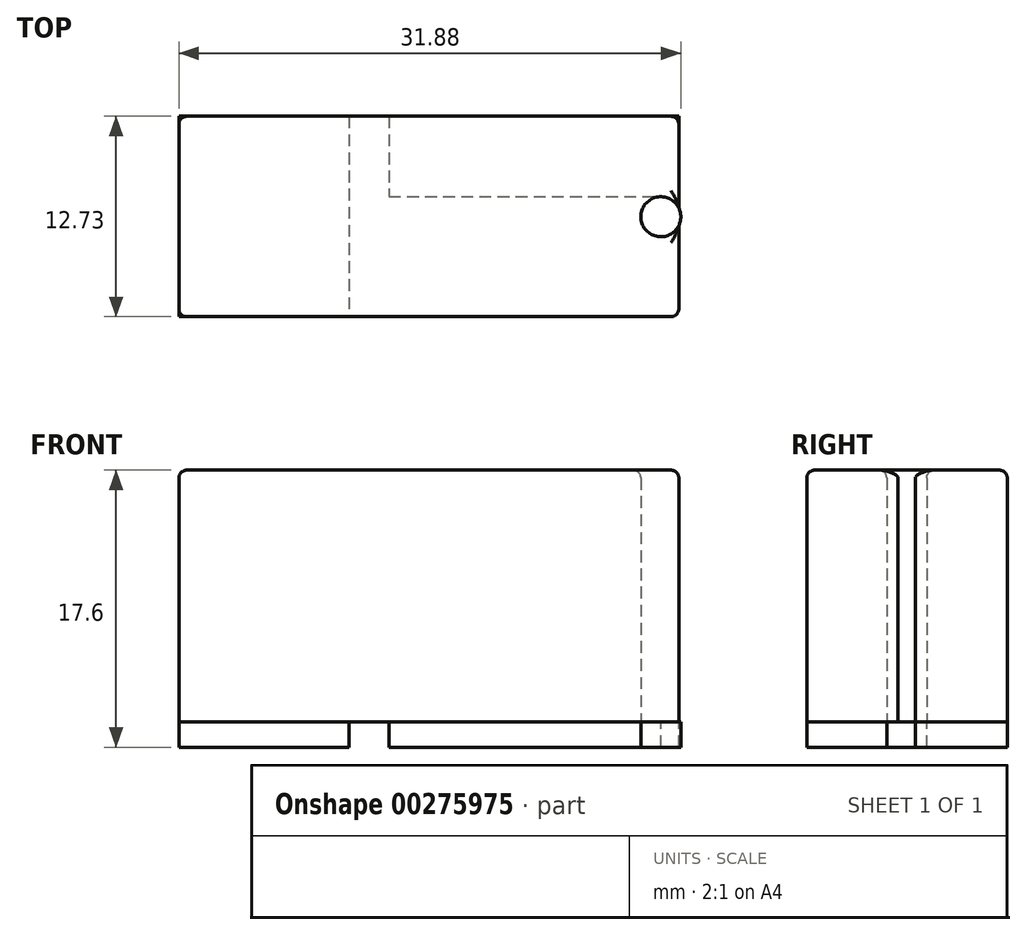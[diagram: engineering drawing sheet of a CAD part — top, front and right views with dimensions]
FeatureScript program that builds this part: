
annotation { "Feature Type Name" : "Feature", "Feature Type Description" : "" }
export const myFeature = defineFeature(function(context is Context, id is Id, definition is map)
    precondition{}
    {
        {
            var Q0;
            Q0=qCreatedBy(makeId("Top.planeOp"),FACE);
            var sketch = newSketch(context, id + "F0", { "sketchPlane" : qUnion([Q0])});
            skLineSegment(sketch, "E0.bottom", {"start": v(-24.13, 16) * mm, "end": v(24.13, 16) * mm});
            skLineSegment(sketch, "E0.top", {"start": v(-24.13, -16) * mm, "end": v(24.13, -16) * mm});
            skLineSegment(sketch, "E0.left", {"start": v(-24.13, 16) * mm, "end": v(-24.13, -16) * mm});
            skLineSegment(sketch, "E0.right", {"start": v(24.13, 16) * mm, "end": v(24.13, -16) * mm});
            skPoint(sketch, "E1", {"position": v(24.13, 0) * mm});
            skPoint(sketch, "E2", {"position": v(0, 16) * mm});
            skSolve(sketch);
        }
        {
            var Q0;
            Q0=makeQuery(id+"F0.imprint","IMPRINT",FACE,{"disambiguationData":[TD([[makeQuery(id+"F0.imprint","IMPRINT",EDGE,{"derivedFrom":sQuery(id+"F0.wireOp",EDGE,"E0.bottom")}),-1.0]])]});
            extrude(context, id + "F1", {"entities" : qUnion([Q0]), "depth" : 1.6 * mm});
        }
        {
            var Q0;
            Q0=makeQuery(id+"F1.opExtrude","CAP_FACE",FACE,{"disambiguationData":[OSD([sQuery(id+"F0.wireOp",EDGE,"E0.bottom"),sQuery(id+"F0.wireOp",EDGE,"E0.top"),sQuery(id+"F0.wireOp",EDGE,"E0.left"),sQuery(id+"F0.wireOp",EDGE,"E0.right")])],"isStart":false});
            var sketch = newSketch(context, id + "F2", { "sketchPlane" : qUnion([Q0])});
            skPoint(sketch, "E3", {"position": v(-14.68, 11.35) * mm});
            skPoint(sketch, "E4", {"position": v(-20.32, -12.2) * mm});
            skLineSegment(sketch, "E5.bottom", {"start": v(-20.32, 6.89) * mm, "end": v(11.43, 6.89) * mm});
            skLineSegment(sketch, "E5.top", {"start": v(-20.32, -5.84) * mm, "end": v(11.43, -5.84) * mm});
            skLineSegment(sketch, "E5.left", {"start": v(-20.32, 6.89) * mm, "end": v(-20.32, -5.84) * mm});
            skLineSegment(sketch, "E5.right", {"start": v(11.43, 6.89) * mm, "end": v(11.43, -5.84) * mm});
            skCircle(sketch, "E6", {"center": v(-8.25, 8.25) * mm, "radius": 1.27 * mm});
            skCircle(sketch, "E7", {"center": v(-8.25, -7.24) * mm, "radius": 1.27 * mm});
            skCircle(sketch, "E8", {"center": v(10.29, 0.5) * mm, "radius": 1.27 * mm});
            skPoint(sketch, "E9", {"position": v(-8.25, 0.5) * mm});
            skLineSegment(sketch, "E10", {"start": v(-8.25, 8.25) * mm, "end": v(-8.25, -7.24) * mm});
            skLineSegment(sketch, "E11", {"start": v(-9.52, 8.25) * mm, "end": v(-9.52, -7.24) * mm});
            skLineSegment(sketch, "E12", {"start": v(-6.98, 8.25) * mm, "end": v(-6.98, 1.78) * mm});
            skLineSegment(sketch, "E13", {"start": v(-6.98, 1.78) * mm, "end": v(10.29, 1.78) * mm});
            skLineSegment(sketch, "E14", {"start": v(10.29, -0.76) * mm, "end": v(-6.98, -0.76) * mm});
            skLineSegment(sketch, "E15", {"start": v(-6.98, -0.76) * mm, "end": v(-6.98, -7.24) * mm});
            skSolve(sketch);
        }
        {
            var Q0;
            {var subQ0=sQuery(id+"F2.wireOp",EDGE,"E11");var subQ1=sQuery(id+"F2.wireOp",EDGE,"E5.bottom");var subQ2=makeQuery(id+"F2.imprint","INTERSECT",VERTEX,{"derivedFrom":[subQ1,subQ0]});Q0=makeQuery(id+"F2.imprint","IMPRINT",FACE,{"disambiguationData":[TD([[makeQuery(id+"F2.imprint","IMPRINT",EDGE,{"disambiguationData":[TD([[subQ2,-1.0]])],"derivedFrom":subQ1}),-1.0]])]});}
            var Q1;
            {var subQ0=sQuery(id+"F2.wireOp",EDGE,"E11");var subQ1=sQuery(id+"F2.wireOp",EDGE,"E5.bottom");var subQ2=makeQuery(id+"F2.imprint","INTERSECT",VERTEX,{"derivedFrom":[subQ1,subQ0]});Q1=makeQuery(id+"F2.imprint","IMPRINT",FACE,{"disambiguationData":[TD([[makeQuery(id+"F2.imprint","IMPRINT",EDGE,{"disambiguationData":[TD([[subQ2,-1.0]])],"derivedFrom":subQ1}),1.0]])]});}
            var Q2;
            {var subQ0=sQuery(id+"F2.wireOp",EDGE,"E6");var subQ1=makeQuery(id+"F2.imprint","INTERSECT",VERTEX,{"derivedFrom":[subQ0,sQuery(id+"F2.wireOp",EDGE,"E11")]});Q2=makeQuery(id+"F2.imprint","IMPRINT",FACE,{"disambiguationData":[TD([[makeQuery(id+"F2.imprint","IMPRINT",EDGE,{"disambiguationData":[TD([[subQ1,1.0]])],"derivedFrom":subQ0}),1.0]])]});}
            var Q3;
            {var subQ0=sQuery(id+"F2.wireOp",EDGE,"E10");var subQ1=sQuery(id+"F2.wireOp",EDGE,"E5.bottom");var subQ2=makeQuery(id+"F2.imprint","INTERSECT",VERTEX,{"derivedFrom":[subQ1,subQ0]});Q3=makeQuery(id+"F2.imprint","IMPRINT",FACE,{"disambiguationData":[TD([[makeQuery(id+"F2.imprint","IMPRINT",EDGE,{"disambiguationData":[TD([[subQ2,-1.0]])],"derivedFrom":subQ1}),1.0]])]});}
            var Q4;
            {var subQ5=sQuery(id+"F2.wireOp",EDGE,"E13");Q4=makeQuery(id+"F2.imprint","IMPRINT",FACE,{"disambiguationData":[TD([[makeQuery(id+"F2.imprint","IMPRINT",EDGE,{"derivedFrom":subQ5}),-1.0]])]});}
            var Q5;
            {var subQ0=sQuery(id+"F2.wireOp",EDGE,"E10");var subQ1=sQuery(id+"F2.wireOp",EDGE,"E5.top");var subQ2=makeQuery(id+"F2.imprint","INTERSECT",VERTEX,{"derivedFrom":[subQ1,subQ0]});Q5=makeQuery(id+"F2.imprint","IMPRINT",FACE,{"disambiguationData":[TD([[makeQuery(id+"F2.imprint","IMPRINT",EDGE,{"disambiguationData":[TD([[subQ2,-1.0]])],"derivedFrom":subQ1}),-1.0]])]});}
            var Q6;
            {var subQ0=sQuery(id+"F2.wireOp",EDGE,"E11");var subQ1=sQuery(id+"F2.wireOp",EDGE,"E5.top");var subQ2=makeQuery(id+"F2.imprint","INTERSECT",VERTEX,{"derivedFrom":[subQ1,subQ0]});Q6=makeQuery(id+"F2.imprint","IMPRINT",FACE,{"disambiguationData":[TD([[makeQuery(id+"F2.imprint","IMPRINT",EDGE,{"disambiguationData":[TD([[subQ2,-1.0]])],"derivedFrom":subQ1}),-1.0]])]});}
            var Q7;
            {var subQ0=sQuery(id+"F2.wireOp",EDGE,"E7");var subQ1=makeQuery(id+"F2.imprint","INTERSECT",VERTEX,{"derivedFrom":[subQ0,sQuery(id+"F2.wireOp",EDGE,"E15")]});Q7=makeQuery(id+"F2.imprint","IMPRINT",FACE,{"disambiguationData":[TD([[makeQuery(id+"F2.imprint","IMPRINT",EDGE,{"disambiguationData":[TD([[subQ1,-1.0]])],"derivedFrom":subQ0}),1.0]])]});}
            var Q8;
            {var subQ0=sQuery(id+"F2.wireOp",EDGE,"E8");var subQ1=sQuery(id+"F2.wireOp",EDGE,"E5.right");var subQ2=makeQuery(id+"F2.imprint","INTERSECT",VERTEX,{"disambiguationData":[OD(0.0)],"derivedFrom":[subQ1,subQ0]});Q8=makeQuery(id+"F2.imprint","IMPRINT",FACE,{"disambiguationData":[TD([[makeQuery(id+"F2.imprint","IMPRINT",EDGE,{"disambiguationData":[TD([[subQ2,-1.0]])],"derivedFrom":subQ1}),-1.0]])]});}
            var Q9;
            {var subQ0=sQuery(id+"F2.wireOp",EDGE,"E8");var subQ1=sQuery(id+"F2.wireOp",EDGE,"E5.right");var subQ2=makeQuery(id+"F2.imprint","INTERSECT",VERTEX,{"disambiguationData":[OD(0.0)],"derivedFrom":[subQ1,subQ0]});Q9=makeQuery(id+"F2.imprint","IMPRINT",FACE,{"disambiguationData":[TD([[makeQuery(id+"F2.imprint","IMPRINT",EDGE,{"disambiguationData":[TD([[subQ2,-1.0]])],"derivedFrom":subQ1}),1.0]])]});}
            extrude(context, id + "F3", {"entities" : qUnion([Q0, Q1, Q2, Q3, Q4, Q5, Q6, Q7, Q8, Q9]), "operationType" : NewBodyOperationType.REMOVE, "endBound" : BoundingType.THROUGH_ALL, "oppositeDirection" : true, "depth" : 25 * mm});
        }
        {
            var Q0;
            {var subQ0=sQuery(id+"F2.wireOp",EDGE,"E5.left");Q0=makeQuery(id+"F2.imprint","IMPRINT",FACE,{"disambiguationData":[TD([[makeQuery(id+"F2.imprint","IMPRINT",EDGE,{"derivedFrom":subQ0}),1.0]])]});}
            var Q1;
            {var subQ0=sQuery(id+"F2.wireOp",EDGE,"E11");var subQ1=sQuery(id+"F2.wireOp",EDGE,"E5.bottom");var subQ2=makeQuery(id+"F2.imprint","INTERSECT",VERTEX,{"derivedFrom":[subQ1,subQ0]});Q1=makeQuery(id+"F2.imprint","IMPRINT",FACE,{"disambiguationData":[TD([[makeQuery(id+"F2.imprint","IMPRINT",EDGE,{"disambiguationData":[TD([[subQ2,-1.0]])],"derivedFrom":subQ1}),-1.0]])]});}
            var Q2;
            {var subQ5=sQuery(id+"F2.wireOp",EDGE,"E13");Q2=makeQuery(id+"F2.imprint","IMPRINT",FACE,{"disambiguationData":[TD([[makeQuery(id+"F2.imprint","IMPRINT",EDGE,{"derivedFrom":subQ5}),-1.0]])]});}
            var Q3;
            {var subQ0=sQuery(id+"F2.wireOp",EDGE,"E13");Q3=makeQuery(id+"F2.imprint","IMPRINT",FACE,{"disambiguationData":[TD([[makeQuery(id+"F2.imprint","IMPRINT",EDGE,{"derivedFrom":subQ0}),1.0]])]});}
            var Q4;
            {var subQ0=sQuery(id+"F2.wireOp",EDGE,"E8");var subQ1=sQuery(id+"F2.wireOp",EDGE,"E5.right");var subQ2=makeQuery(id+"F2.imprint","INTERSECT",VERTEX,{"disambiguationData":[OD(0.0)],"derivedFrom":[subQ1,subQ0]});Q4=makeQuery(id+"F2.imprint","IMPRINT",FACE,{"disambiguationData":[TD([[makeQuery(id+"F2.imprint","IMPRINT",EDGE,{"disambiguationData":[TD([[subQ2,-1.0]])],"derivedFrom":subQ1}),-1.0]])]});}
            var Q5;
            {var subQ0=sQuery(id+"F2.wireOp",EDGE,"E14");Q5=makeQuery(id+"F2.imprint","IMPRINT",FACE,{"disambiguationData":[TD([[makeQuery(id+"F2.imprint","IMPRINT",EDGE,{"derivedFrom":subQ0}),1.0]])]});}
            extrude(context, id + "F4", {"entities" : qUnion([Q0, Q1, Q2, Q3, Q4, Q5]), "depth" : 16 * mm});
        }
        {
            var Q0;
            Q0=makeQuery(id+"F4.opExtrude","CAP_FACE",FACE,{"disambiguationData":[OSD([sQuery(id+"F2.wireOp",EDGE,"E5.bottom"),sQuery(id+"F2.wireOp",EDGE,"E5.top"),sQuery(id+"F2.wireOp",EDGE,"E5.left"),sQuery(id+"F2.wireOp",EDGE,"E5.right")])],"isStart":false});
            var Q1;
            Q1=makeQuery(id+"F4.opExtrude","SWEPT_EDGE",EDGE,{"disambiguationData":[OSD([sQuery(id+"F2.wireOp",EDGE,"E5.top"),sQuery(id+"F2.wireOp",EDGE,"E5.left")])]});
            var Q2;
            Q2=makeQuery(id+"F4.opExtrude","SWEPT_EDGE",EDGE,{"disambiguationData":[OSD([sQuery(id+"F2.wireOp",EDGE,"E5.top"),sQuery(id+"F2.wireOp",EDGE,"E5.right")])]});
            var Q3;
            Q3=makeQuery(id+"F4.opExtrude","SWEPT_EDGE",EDGE,{"disambiguationData":[OSD([sQuery(id+"F2.wireOp",EDGE,"E5.bottom"),sQuery(id+"F2.wireOp",EDGE,"E5.right")])]});
            var Q4;
            Q4=makeQuery(id+"F4.opExtrude","SWEPT_EDGE",EDGE,{"disambiguationData":[OSD([sQuery(id+"F2.wireOp",EDGE,"E5.bottom"),sQuery(id+"F2.wireOp",EDGE,"E5.left")])]});
            fillet(context, id + "F5", {"entities" : qUnion([Q0, Q1, Q2, Q3, Q4]), "radius" : 0.5 * mm, "tangentPropagation" : true, "allowEdgeOverflow" : false});
        }
        {
            var Q0;
            Q0=sQuery(id+"F2.wireOp",VERTEX,"E3");
            var Q1;
            Q1=sQuery(id+"F2.wireOp",VERTEX,"E4");
            var Q2;
            Q2=makeQuery(id+"F1.opExtrude","SWEPT_BODY",BODY,{"disambiguationData":[OSD([sQuery(id+"F0.wireOp",EDGE,"E0.bottom"),sQuery(id+"F0.wireOp",EDGE,"E0.top"),sQuery(id+"F0.wireOp",EDGE,"E0.left"),sQuery(id+"F0.wireOp",EDGE,"E0.right")])]});
            hole(context, id + "F6", {"style" : HoleStyle.SIMPLE, "endStyle" : HoleEndStyle.THROUGH, "standardTappedOrClearance" : lookupTablePath({ "standard" : "ISO", "fit" : "Normal", "size" : "M3", "type" : "Clearance" }), "standardBlindInLast" : lookupTablePath({ "fit" : "Standard", "standard" : "ISO", "size" : "M3", "type" : "Clearance" }), "holeDiameter" : 3.3 * mm, "tappedDepth" : 13.2 * mm, "tapClearance" : 3, "startFromSketch" : true, "locations" : qUnion([Q0, Q1]), "scope" : qUnion([Q2])});
        }
    });
